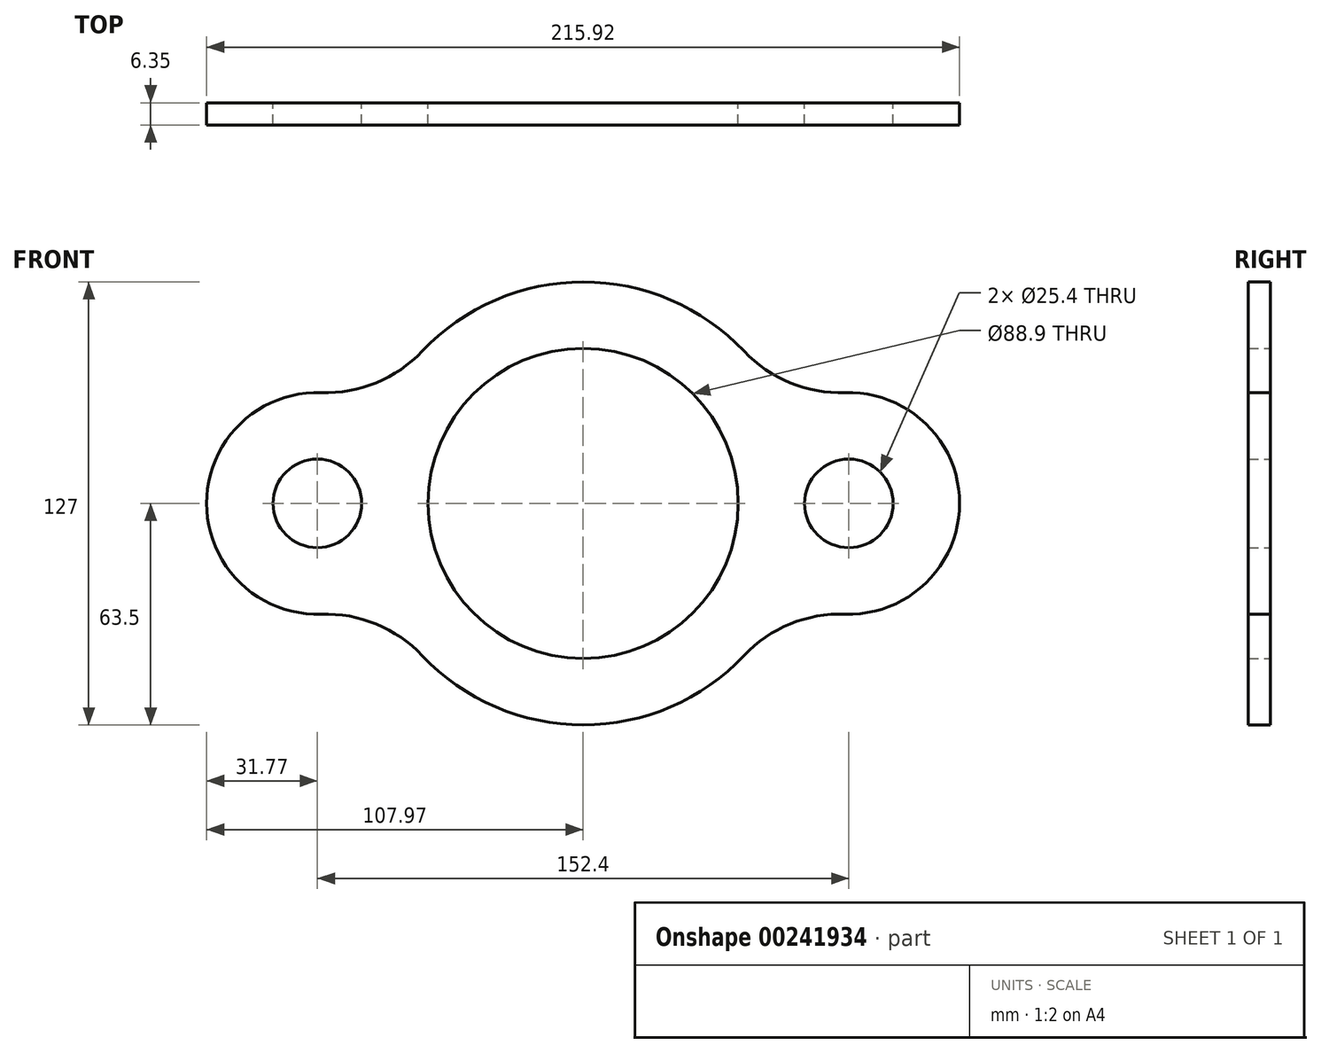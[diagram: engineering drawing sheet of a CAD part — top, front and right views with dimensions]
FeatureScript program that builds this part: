
annotation { "Feature Type Name" : "Feature", "Feature Type Description" : "" }
export const myFeature = defineFeature(function(context is Context, id is Id, definition is map)
    precondition{}
    {
        {
            var Q0;
            Q0=qCreatedBy(makeId("Front.planeOp"),FACE);
            var sketch = newSketch(context, id + "F0", { "sketchPlane" : qUnion([Q0])});
            skCircle(sketch, "E0", {"center": v(0, 0) * mm, "radius": 44.45 * mm});
            skArc(sketch, "E1", {"start": v(-46.13, -43.64) * mm, "mid": v(0, -63.5) * mm, "end": v(46.14, -43.63) * mm});
            skCircle(sketch, "E2", {"center": v(-76.2, 0) * mm, "radius": 12.7 * mm});
            skCircle(sketch, "E3", {"center": v(76.2, 0) * mm, "radius": 12.7 * mm});
            skArc(sketch, "E4", {"start": v(75.12, -31.73) * mm, "mid": v(107.95, 0) * mm, "end": v(75.12, 31.73) * mm});
            skArc(sketch, "E5", {"start": v(-75.1, 31.75) * mm, "mid": v(-107.97, 0) * mm, "end": v(-75.1, -31.75) * mm});
            skArc(sketch, "E6.trimOffspring", {"start": v(-44.44, -0.84) * mm, "mid": v(-44.43, 0) * mm, "end": v(-44.44, 0.84) * mm});
            skArc(sketch, "E7.trimOffspring", {"start": v(46.14, 43.63) * mm, "mid": v(0, 63.5) * mm, "end": v(-46.13, 43.64) * mm});
            skPoint(sketch, "E8.visualSharp", {"position": v(-57.94, 26) * mm});
            skArc(sketch, "E8.filletArc", {"start": v(-75.1, 31.75) * mm, "mid": v(-59.34, 34.58) * mm, "end": v(-46.13, 43.64) * mm});
            skPoint(sketch, "E9.visualSharp", {"position": v(-57.94, -26) * mm});
            skArc(sketch, "E9.filletArc", {"start": v(-46.13, -43.64) * mm, "mid": v(-59.34, -34.58) * mm, "end": v(-75.1, -31.75) * mm});
            skPoint(sketch, "E10.visualSharp", {"position": v(57.94, -25.98) * mm});
            skArc(sketch, "E10.filletArc", {"start": v(75.12, -31.73) * mm, "mid": v(59.35, -34.56) * mm, "end": v(46.14, -43.63) * mm});
            skPoint(sketch, "E11.visualSharp", {"position": v(57.94, 25.98) * mm});
            skArc(sketch, "E11.filletArc", {"start": v(46.14, 43.63) * mm, "mid": v(59.35, 34.56) * mm, "end": v(75.12, 31.73) * mm});
            skSolve(sketch);
        }
        {
            var Q0;
            Q0=makeQuery(id+"F0.imprint","IMPRINT",FACE,{"disambiguationData":[TD([[makeQuery(id+"F0.imprint","IMPRINT",EDGE,{"derivedFrom":sQuery(id+"F0.wireOp",EDGE,"E1")}),1.0]])]});
            extrude(context, id + "F1", {"entities" : qUnion([Q0]), "depth" : 6.35 * mm});
        }
    });
